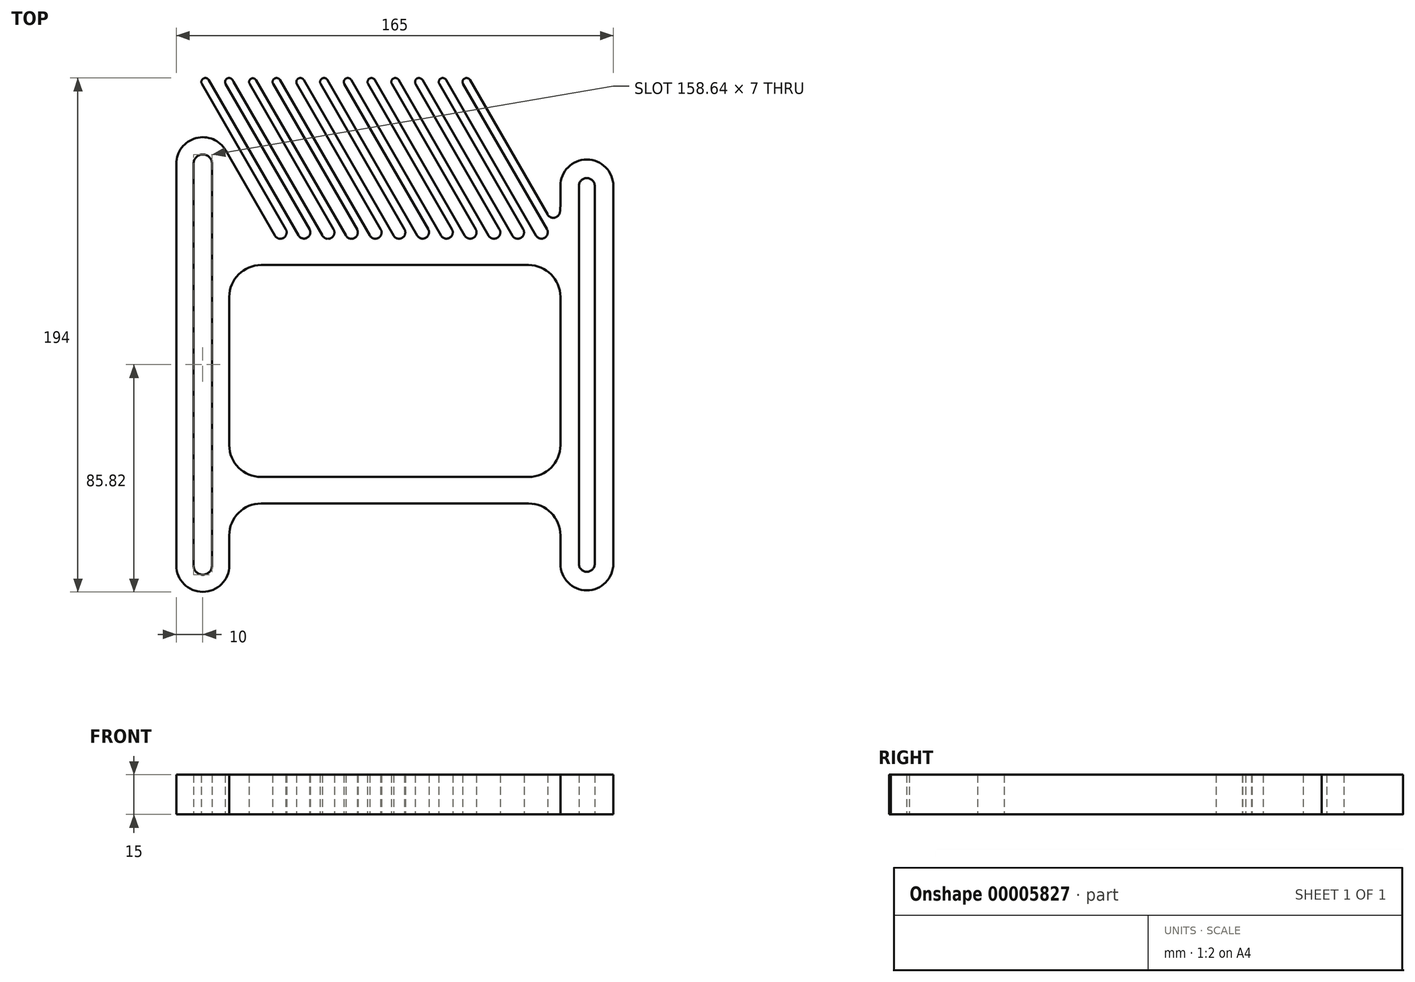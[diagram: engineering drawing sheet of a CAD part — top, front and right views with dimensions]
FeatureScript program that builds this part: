
annotation { "Feature Type Name" : "Feature", "Feature Type Description" : "" }
export const myFeature = defineFeature(function(context is Context, id is Id, definition is map)
    precondition{}
    {
        {
            var Q0;
            Q0=qCreatedBy(makeId("Top.planeOp"),FACE);
            var sketch = newSketch(context, id + "F0", { "sketchPlane" : qUnion([Q0])});
            skLineSegment(sketch, "E0.left", {"start": v(-82.5, 75.82) * mm, "end": v(-82.5, -75.82) * mm});
            skLineSegment(sketch, "E0.right", {"start": v(-62.5, 25.57) * mm, "end": v(-62.5, -30.43) * mm});
            skArc(sketch, "E1", {"start": v(-63.84, 80.82) * mm, "mid": v(-75.09, 85.48) * mm, "end": v(-82.5, 75.82) * mm});
            skArc(sketch, "E2", {"start": v(-82.5, -75.82) * mm, "mid": v(-72.5, -85.82) * mm, "end": v(-62.5, -75.82) * mm});
            skLineSegment(sketch, "E3.left", {"start": v(62.5, 67.42) * mm, "end": v(62.5, 59.57) * mm});
            skLineSegment(sketch, "E3.right", {"start": v(82.5, 67.42) * mm, "end": v(82.5, -75.2) * mm});
            skArc(sketch, "E4", {"start": v(82.5, 67.42) * mm, "mid": v(72.5, 77.42) * mm, "end": v(62.5, 67.42) * mm});
            skArc(sketch, "E5", {"start": v(62.5, -75.2) * mm, "mid": v(72.5, -85.2) * mm, "end": v(82.5, -75.2) * mm});
            skLineSegment(sketch, "E6.top", {"start": v(50.5, 37.57) * mm, "end": v(-50.5, 37.57) * mm});
            skLineSegment(sketch, "E7.bottom", {"start": v(-50.5, -42.43) * mm, "end": v(50.5, -42.43) * mm});
            skLineSegment(sketch, "E7.top", {"start": v(-50.5, -52.43) * mm, "end": v(50.5, -52.43) * mm});
            skLineSegment(sketch, "E7.right", {"start": v(62.5, -42.43) * mm, "end": v(62.5, -52.39) * mm});
            skLineSegment(sketch, "E8", {"start": v(72.5, 67.42) * mm, "end": v(72.5, -75.2) * mm, "construction": true});
            skLineSegment(sketch, "E9", {"start": v(-72.5, -75.82) * mm, "end": v(-72.5, 75.82) * mm, "construction": true});
            skArc(sketch, "E10.0.startCap", {"start": v(-69, -75.82) * mm, "mid": v(-72.5, -79.32) * mm, "end": v(-76, -75.82) * mm});
            skArc(sketch, "E10.0.endCap", {"start": v(-76, 75.82) * mm, "mid": v(-72.5, 79.32) * mm, "end": v(-69, 75.82) * mm});
            skLineSegment(sketch, "E10.0.left", {"start": v(-76, -75.82) * mm, "end": v(-76, 75.82) * mm});
            skLineSegment(sketch, "E10.0.right", {"start": v(-69, -75.82) * mm, "end": v(-69, 75.82) * mm});
            skArc(sketch, "E11.0.startCap", {"start": v(69.5, 67.42) * mm, "mid": v(72.5, 70.42) * mm, "end": v(75.5, 67.42) * mm});
            skArc(sketch, "E11.0.endCap", {"start": v(75.5, -75.2) * mm, "mid": v(72.5, -78.2) * mm, "end": v(69.5, -75.2) * mm});
            skLineSegment(sketch, "E11.0.left", {"start": v(75.5, 67.42) * mm, "end": v(75.5, -75.2) * mm});
            skLineSegment(sketch, "E11.0.right", {"start": v(69.5, 67.42) * mm, "end": v(69.5, -75.2) * mm});
            skLineSegment(sketch, "E12", {"start": v(62.5, -75.2) * mm, "end": v(82.5, -75.2) * mm, "construction": true});
            skLineSegment(sketch, "E13", {"start": v(-63.84, 80.82) * mm, "end": v(-45.3, 48.7) * mm});
            skLineSegment(sketch, "E14", {"start": v(-72.84, 105.93) * mm, "end": v(-41.2, 51.14) * mm});
            skLineSegment(sketch, "E15.0", {"start": v(-70.24, 107.43) * mm, "end": v(-36.36, 48.75) * mm});
            skArc(sketch, "E16", {"start": v(-70.24, 107.43) * mm, "mid": v(-72.29, 107.98) * mm, "end": v(-72.84, 105.93) * mm});
            skLineSegment(sketch, "E17.1.0.0", {"start": v(-63.87, 105.93) * mm, "end": v(-32.17, 51.02) * mm});
            skLineSegment(sketch, "E17.1.0.1", {"start": v(-61.27, 107.43) * mm, "end": v(-60.84, 106.68) * mm});
            skArc(sketch, "E17.1.0.2", {"start": v(-61.27, 107.43) * mm, "mid": v(-63.32, 107.98) * mm, "end": v(-63.87, 105.93) * mm});
            skLineSegment(sketch, "E17.2.0.0", {"start": v(-54.82, 105.98) * mm, "end": v(-23.13, 51.1) * mm});
            skArc(sketch, "E17.2.0.2", {"start": v(-52.4, 107.37) * mm, "mid": v(-54.3, 107.88) * mm, "end": v(-54.82, 105.98) * mm});
            skLineSegment(sketch, "E17.3.0.0", {"start": v(-45.94, 105.93) * mm, "end": v(-14.2, 50.94) * mm});
            skLineSegment(sketch, "E17.3.0.1", {"start": v(-43.35, 107.43) * mm, "end": v(-9.46, 48.73) * mm});
            skArc(sketch, "E17.3.0.2", {"start": v(-43.35, 107.43) * mm, "mid": v(-45.4, 107.98) * mm, "end": v(-45.94, 105.93) * mm});
            skLineSegment(sketch, "E17.4.0.0", {"start": v(-36.98, 105.93) * mm, "end": v(-5.33, 51.12) * mm});
            skLineSegment(sketch, "E17.4.0.1", {"start": v(-34.38, 107.43) * mm, "end": v(-0.5, 48.73) * mm});
            skArc(sketch, "E17.4.0.2", {"start": v(-34.38, 107.43) * mm, "mid": v(-36.43, 107.98) * mm, "end": v(-36.98, 105.93) * mm});
            skLineSegment(sketch, "E17.5.0.0", {"start": v(-28.02, 105.93) * mm, "end": v(3.63, 51.11) * mm});
            skLineSegment(sketch, "E17.5.0.1", {"start": v(-25.42, 107.43) * mm, "end": v(8.48, 48.72) * mm});
            skArc(sketch, "E17.5.0.2", {"start": v(-25.42, 107.43) * mm, "mid": v(-27.47, 107.98) * mm, "end": v(-28.02, 105.93) * mm});
            skLineSegment(sketch, "E17.6.0.0", {"start": v(-19.05, 105.93) * mm, "end": v(12.6, 51.1) * mm});
            skLineSegment(sketch, "E17.6.0.1", {"start": v(-16.45, 107.43) * mm, "end": v(17.44, 48.72) * mm});
            skArc(sketch, "E17.6.0.2", {"start": v(-16.45, 107.43) * mm, "mid": v(-18.5, 107.98) * mm, "end": v(-19.05, 105.93) * mm});
            skLineSegment(sketch, "E17.7.0.0", {"start": v(-10.09, 105.93) * mm, "end": v(21.57, 51.1) * mm});
            skLineSegment(sketch, "E17.7.0.1", {"start": v(-7.49, 107.43) * mm, "end": v(26.4, 48.71) * mm});
            skArc(sketch, "E17.7.0.2", {"start": v(-7.49, 107.43) * mm, "mid": v(-9.54, 107.98) * mm, "end": v(-10.09, 105.93) * mm});
            skLineSegment(sketch, "E17.8.0.0", {"start": v(-1.12, 105.93) * mm, "end": v(30.53, 51.1) * mm});
            skLineSegment(sketch, "E17.8.0.1", {"start": v(1.48, 107.43) * mm, "end": v(35.38, 48.7) * mm});
            skArc(sketch, "E17.8.0.2", {"start": v(1.48, 107.43) * mm, "mid": v(-0.57, 107.98) * mm, "end": v(-1.12, 105.93) * mm});
            skLineSegment(sketch, "E17.9.0.0", {"start": v(7.84, 105.93) * mm, "end": v(39.5, 51.09) * mm});
            skLineSegment(sketch, "E17.9.0.1", {"start": v(10.44, 107.43) * mm, "end": v(44.34, 48.7) * mm});
            skArc(sketch, "E17.9.0.2", {"start": v(10.44, 107.43) * mm, "mid": v(8.4, 107.98) * mm, "end": v(7.84, 105.93) * mm});
            skLineSegment(sketch, "E17.10.0.0", {"start": v(16.8, 105.93) * mm, "end": v(48.47, 51.08) * mm});
            skLineSegment(sketch, "E17.10.0.1", {"start": v(19.4, 107.43) * mm, "end": v(53.31, 48.7) * mm});
            skArc(sketch, "E17.10.0.2", {"start": v(19.4, 107.43) * mm, "mid": v(17.35, 107.98) * mm, "end": v(16.8, 105.93) * mm});
            skLineSegment(sketch, "E17.11.0.0", {"start": v(25.77, 105.93) * mm, "end": v(57.44, 51.08) * mm});
            skLineSegment(sketch, "E17.11.0.1", {"start": v(28.37, 107.43) * mm, "end": v(57.69, 56.64) * mm});
            skArc(sketch, "E17.11.0.2", {"start": v(28.37, 107.43) * mm, "mid": v(26.32, 107.98) * mm, "end": v(25.77, 105.93) * mm});
            skLineSegment(sketch, "E18.filletArc", {"start": v(47.06, 60.31) * mm, "end": v(47.06, 60.31) * mm});
            skArc(sketch, "E19.filletArc", {"start": v(-62.5, -30.43) * mm, "mid": v(-58.99, -38.92) * mm, "end": v(-50.5, -42.43) * mm});
            skLineSegment(sketch, "E20", {"start": v(-62.5, -75.82) * mm, "end": v(-62.5, -64.43) * mm});
            skPoint(sketch, "E21.visualSharp", {"position": v(-62.5, -52.43) * mm});
            skArc(sketch, "E21.filletArc", {"start": v(-50.5, -52.43) * mm, "mid": v(-58.99, -55.95) * mm, "end": v(-62.5, -64.43) * mm});
            skLineSegment(sketch, "E22", {"start": v(62.5, -75.2) * mm, "end": v(62.5, -64.43) * mm});
            skArc(sketch, "E23.filletArc", {"start": v(62.5, -64.43) * mm, "mid": v(58.99, -55.95) * mm, "end": v(50.5, -52.43) * mm});
            skLineSegment(sketch, "E24", {"start": v(62.5, -30.43) * mm, "end": v(62.5, 25.57) * mm});
            skPoint(sketch, "E25.visualSharp", {"position": v(62.5, -42.43) * mm});
            skArc(sketch, "E25.filletArc", {"start": v(50.5, -42.43) * mm, "mid": v(58.99, -38.92) * mm, "end": v(62.5, -30.43) * mm});
            skArc(sketch, "E26.filletArc", {"start": v(62.5, 25.57) * mm, "mid": v(58.99, 34.05) * mm, "end": v(50.5, 37.57) * mm});
            skArc(sketch, "E27.filletArc", {"start": v(-50.5, 37.57) * mm, "mid": v(-58.99, 34.05) * mm, "end": v(-62.5, 25.57) * mm});
            skArc(sketch, "E28.trimOffspring", {"start": v(62.31, 57.45) * mm, "mid": v(62.45, 58.5) * mm, "end": v(62.5, 59.57) * mm});
            skLineSegment(sketch, "E29", {"start": v(-72.84, 105.93) * mm, "end": v(-70.24, 107.43) * mm, "construction": true});
            skLineSegment(sketch, "E30", {"start": v(-71.54, 106.68) * mm, "end": v(47, 106.68) * mm, "construction": true});
            skArc(sketch, "E31", {"start": v(-45.3, 48.7) * mm, "mid": v(-42, 47.84) * mm, "end": v(-41.2, 51.14) * mm});
            skArc(sketch, "E32.2.0.0", {"start": v(-27.39, 48.75) * mm, "mid": v(-24.06, 47.76) * mm, "end": v(-23.13, 51.1) * mm});
            skArc(sketch, "E33.0.3.0", {"start": v(-18.5, 48.78) * mm, "mid": v(-15.28, 47.74) * mm, "end": v(-14.2, 50.94) * mm});
            skArc(sketch, "E33.0.4.0", {"start": v(-9.46, 48.73) * mm, "mid": v(-6.18, 47.82) * mm, "end": v(-5.33, 51.12) * mm});
            skArc(sketch, "E33.0.5.0", {"start": v(-0.5, 48.73) * mm, "mid": v(2.78, 47.82) * mm, "end": v(3.63, 51.11) * mm});
            skArc(sketch, "E33.0.6.0", {"start": v(8.48, 48.72) * mm, "mid": v(11.73, 47.85) * mm, "end": v(12.6, 51.1) * mm});
            skArc(sketch, "E33.0.7.0", {"start": v(17.44, 48.72) * mm, "mid": v(20.7, 47.85) * mm, "end": v(21.57, 51.1) * mm});
            skArc(sketch, "E33.0.8.0", {"start": v(26.4, 48.71) * mm, "mid": v(29.66, 47.84) * mm, "end": v(30.53, 51.1) * mm});
            skArc(sketch, "E33.0.9.0", {"start": v(35.38, 48.7) * mm, "mid": v(38.64, 47.82) * mm, "end": v(39.5, 51.09) * mm});
            skArc(sketch, "E33.0.10.0", {"start": v(44.34, 48.7) * mm, "mid": v(47.6, 47.82) * mm, "end": v(48.47, 51.08) * mm});
            skArc(sketch, "E33.0.11.0", {"start": v(53.31, 48.7) * mm, "mid": v(56.57, 47.82) * mm, "end": v(57.44, 51.08) * mm});
            skPoint(sketch, "E34.trimOffspring.end.orphan", {"position": v(-39.14, 47.57) * mm});
            skLineSegment(sketch, "E35.trimOffspring", {"start": v(-39.8, 61.5) * mm, "end": v(-39.8, 61.5) * mm});
            skPoint(sketch, "E36.orphan", {"position": v(-44.64, 47.57) * mm});
            skLineSegment(sketch, "E37", {"start": v(-27.39, 48.75) * mm, "end": v(-60.84, 106.68) * mm});
            skLineSegment(sketch, "E38", {"start": v(-18.5, 48.78) * mm, "end": v(-52.4, 107.37) * mm});
            skArc(sketch, "E39.filletArc", {"start": v(57.69, 56.64) * mm, "mid": v(60.28, 55.43) * mm, "end": v(62.31, 57.45) * mm});
            skLineSegment(sketch, "E40", {"start": v(-43.23, 49.89) * mm, "end": v(55.37, 49.89) * mm, "construction": true});
            skArc(sketch, "E41", {"start": v(-36.36, 48.75) * mm, "mid": v(-33.16, 47.85) * mm, "end": v(-32.17, 51.02) * mm});
            skPoint(sketch, "E42", {"position": v(0, 0) * mm});
            skSolve(sketch);
        }
        {
            var Q0;
            Q0=makeQuery(id+"F0.imprint","IMPRINT",FACE,{"disambiguationData":[TD([[makeQuery(id+"F0.imprint","IMPRINT",EDGE,{"derivedFrom":sQuery(id+"F0.wireOp",EDGE,"E0.left")}),1.0]])]});
            extrude(context, id + "F1", {"entities" : qUnion([Q0]), "depth" : 15 * mm, "offsetDistance" : 25 * mm});
        }
    });
